# Revit family: Haworth_CabanaLounge_CollaborativeSofa_TwoArms_EU_PRELIMINARY
name_source: partatom
category: Furniture
revit_build: Autodesk Revit 2018 (Build: 20170223_1515(x64)
units: mm (PartAtom-declared; Revit-internal decimal feet)

## family parameters
Always vertical = Yes
Cut with Voids When Loaded = No
OmniClass Number = 23.40.70.14.64.21
OmniClass Title = Systems Furniture
Room Calculation Point = No
Shared = No
Work Plane-Based = No

## types (6) — shared parameters
Assembly Code = E2020200
Description = Haworth - Cabana Lounge - Collaborative Sofa - Two Arms
Leg Offset = 7 cm
Manufacturer = Haworth
Model = SECBTA
Revision Number = 1
Screen Width = 97 cm
Seat Depth = 76 cm
Seat Height = 46 cm
Seat Width = 183 cm
Size = Verify Final Dim. w/ Haworth
URL = https://www.haworth.com
URL - Product = https://www.haworth.com
Warranty = http://www.haworth.com

## per-type parameters (varying)
| type | Actual Depth | Actual Height | Actual Width | Alignment Clip Control | High Screen | Low Screen | No Screen | With Screen | With Top |
| Two Seats - High Screen - With Integrated Table | 81 cm | 137 cm | 193 cm | Yes | Yes | No | No | Yes | Yes |
| Two Seats - Low Screen - With Integrated Table | 81 cm | 107 cm | 193 cm | Yes | No | Yes | No | Yes | Yes |
| Two Seats - High Screen - Without Integrated Table | 81 cm | 137 cm | 193 cm | Yes | Yes | No | No | Yes | No |
| Two Seats - Low Screen - Without Integrated Table | 81 cm | 107 cm | 193 cm | Yes | No | Yes | No | Yes | No |
| Two Seats - No Screen - Without Integrated Table | 76 cm | 77 cm | 183 cm | No | No | No | Yes | No | No |
| Two Seats - No Screen - With Integrated Table | 76 cm | 77 cm | 183 cm | No | No | No | Yes | No | Yes |

## geometry (parser evidence)
native form markers: Extrusion x1, Sweep x12
no freeform markers — native parametric forms only
